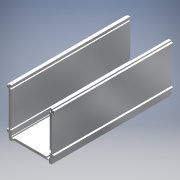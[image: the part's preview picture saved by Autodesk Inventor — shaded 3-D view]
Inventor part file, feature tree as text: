
AUTODESK INVENTOR PART (.ipt)
format: ipt  version: 2019 (Build 230136000, 136)  size: 180,736 bytes
history: native  units: in
note: dims shown in document units (in); Inventor stores cm internally (conversion verified against a paired STEP export)
features: extrude x1, sketch x1
ambient origin geometry x8: Origin, YZ Plane, XZ Plane, XY Plane, X Axis, Y Axis, Z Axis, Center Point
bodies: Solid1 (feature_tree)
feature tree (2):
  extrude  "Extrusion1"  Depth=4.375in
  sketch  "Sketch1"  dims[d0=4.6875in d1=4.375in d2=0.25in d3=4.4375in d4=3.875in d5=12.0in d6=0.0in d7=4.6875in d8=0.125in d9=0.125in d10=0.125in d11=0.188in d12=0.25in d13=0.438in d14=0.188in d15=0.25in d16=0.0625in d17=0.188in d18=0.25in d19=0.188in d20=0.188in d21=0.0625in d22=0.25in d23=0.25in d24=0.125in d25=0.125in d26=0.5in d27=0.25in d28=0.0625in d29=0.125in d30=0.25in d31=0.0625in d32=0.25in d33=0.5in d34=0.25in]
